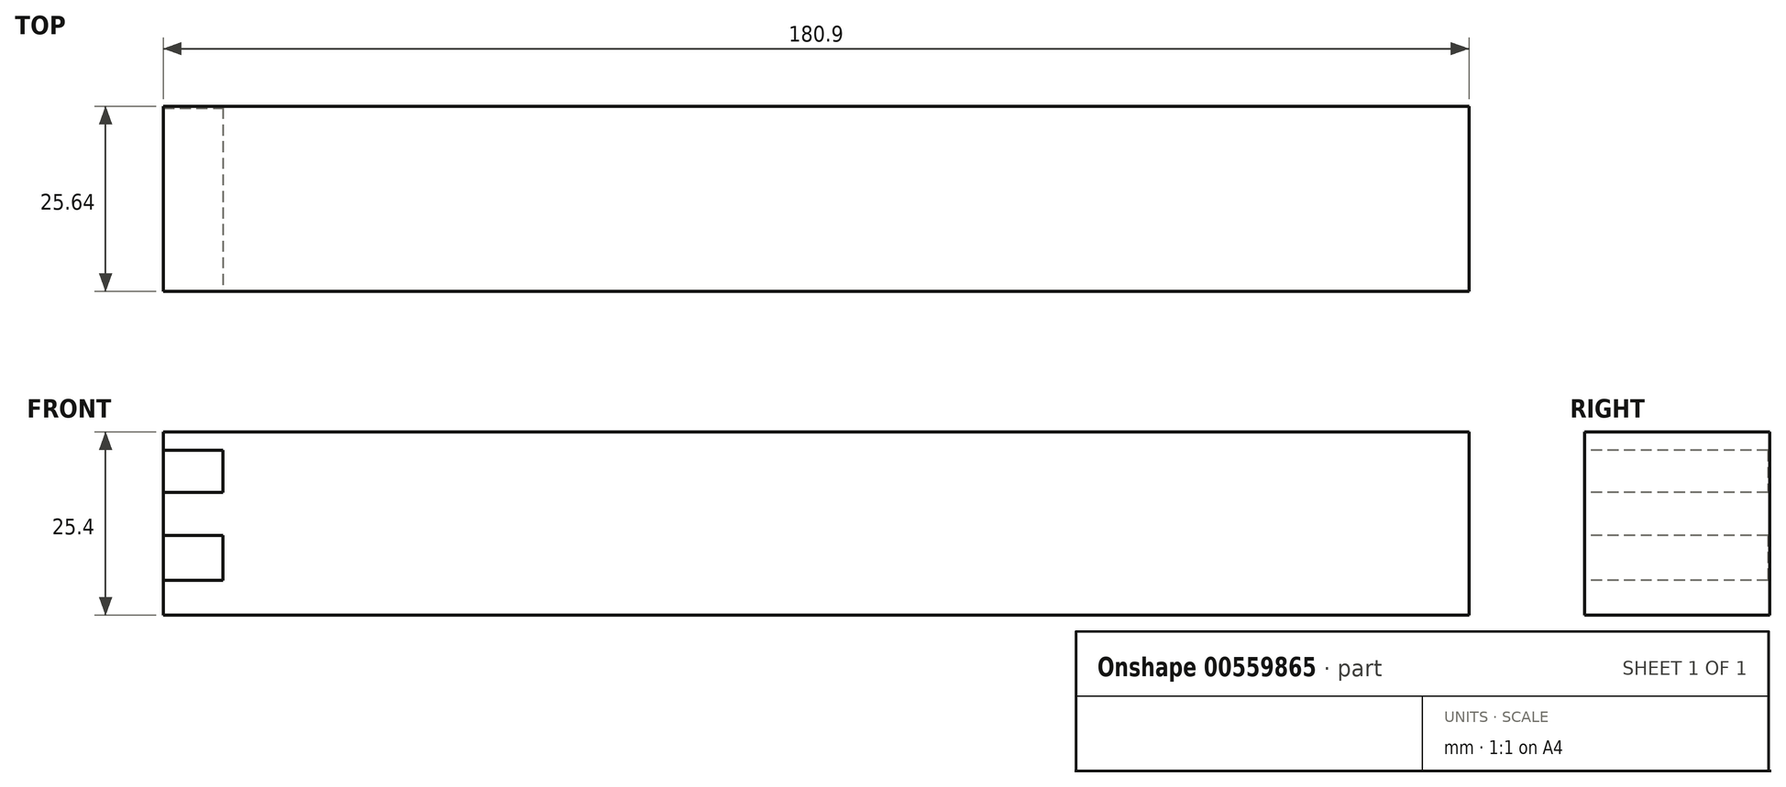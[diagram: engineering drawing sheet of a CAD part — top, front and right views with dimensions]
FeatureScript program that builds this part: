
annotation { "Feature Type Name" : "Feature", "Feature Type Description" : "" }
export const myFeature = defineFeature(function(context is Context, id is Id, definition is map)
    precondition{}
    {
        {
            var Q0;
            Q0=qCreatedBy(makeId("Top.planeOp"),FACE);
            var sketch = newSketch(context, id + "F0", { "sketchPlane" : qUnion([Q0])});
            skLineSegment(sketch, "E0.bottom", {"start": v(-57.58, 23.57) * mm, "end": v(123.32, 23.57) * mm});
            skLineSegment(sketch, "E0.top", {"start": v(-57.58, -2.07) * mm, "end": v(123.32, -2.07) * mm});
            skLineSegment(sketch, "E0.left", {"start": v(-57.58, 23.57) * mm, "end": v(-57.58, -2.07) * mm});
            skLineSegment(sketch, "E0.right", {"start": v(123.32, 23.57) * mm, "end": v(123.32, -2.07) * mm});
            skSolve(sketch);
        }
        {
            var Q0;
            Q0=makeQuery(id+"F0.imprint","IMPRINT",FACE,{"disambiguationData":[TD([[makeQuery(id+"F0.imprint","IMPRINT",EDGE,{"derivedFrom":sQuery(id+"F0.wireOp",EDGE,"E0.bottom")}),-1.0]])]});
            extrude(context, id + "F1", {"entities" : qUnion([Q0]), "depth" : 25.4 * mm, "offsetDistance" : 25.4 * mm});
        }
        {
            var Q0;
            Q0=makeQuery(id+"F1.opExtrude","SWEPT_FACE",FACE,{"disambiguationData":[OSD([sQuery(id+"F0.wireOp",EDGE,"E0.top")])]});
            var sketch = newSketch(context, id + "F2", { "sketchPlane" : qUnion([Q0])});
            skLineSegment(sketch, "E1", {"start": v(-57.58, 4.84) * mm, "end": v(-49.32, 4.84) * mm});
            skLineSegment(sketch, "E2", {"start": v(-49.32, 4.84) * mm, "end": v(-49.32, 11.05) * mm});
            skLineSegment(sketch, "E3", {"start": v(-49.32, 11.05) * mm, "end": v(-57.58, 11.05) * mm});
            skLineSegment(sketch, "E4", {"start": v(-57.58, 11.05) * mm, "end": v(-57.58, 17.04) * mm});
            skLineSegment(sketch, "E5", {"start": v(-57.58, 17.04) * mm, "end": v(-49.32, 17.04) * mm});
            skLineSegment(sketch, "E6", {"start": v(-49.32, 17.04) * mm, "end": v(-49.32, 22.83) * mm});
            skLineSegment(sketch, "E7", {"start": v(-49.32, 22.83) * mm, "end": v(-57.58, 22.83) * mm});
            skLineSegment(sketch, "E8", {"start": v(-57.58, 22.83) * mm, "end": v(-57.58, 4.84) * mm});
            skSolve(sketch);
        }
        {
            var Q0;
            Q0=makeQuery(id+"F1.opExtrude","SWEPT_FACE",FACE,{"disambiguationData":[OSD([sQuery(id+"F0.wireOp",EDGE,"E0.bottom")])]});
            var Q1;
            {var subQ0=sQuery(id+"F2.wireOp",EDGE,"E5");Q1=makeQuery(id+"F2.imprint","IMPRINT",FACE,{"disambiguationData":[TD([[makeQuery(id+"F2.imprint","IMPRINT",EDGE,{"derivedFrom":subQ0}),1.0]])]});}
            extrude(context, id + "F3", {"entities" : qUnion([Q0, Q1]), "operationType" : NewBodyOperationType.INTERSECT, "endBound" : BoundingType.THROUGH_ALL, "oppositeDirection" : true, "depth" : 25.4 * mm, "offsetDistance" : 25.4 * mm});
        }
        {
            var Q0;
            Q0 = qSketchRegion(id + "F2", true);
            extrude(context, id + "F4", {"entities" : qUnion([Q0]), "operationType" : NewBodyOperationType.REMOVE, "oppositeDirection" : true, "depth" : 25.4 * mm, "offsetDistance" : 25.4 * mm});
        }
    });
